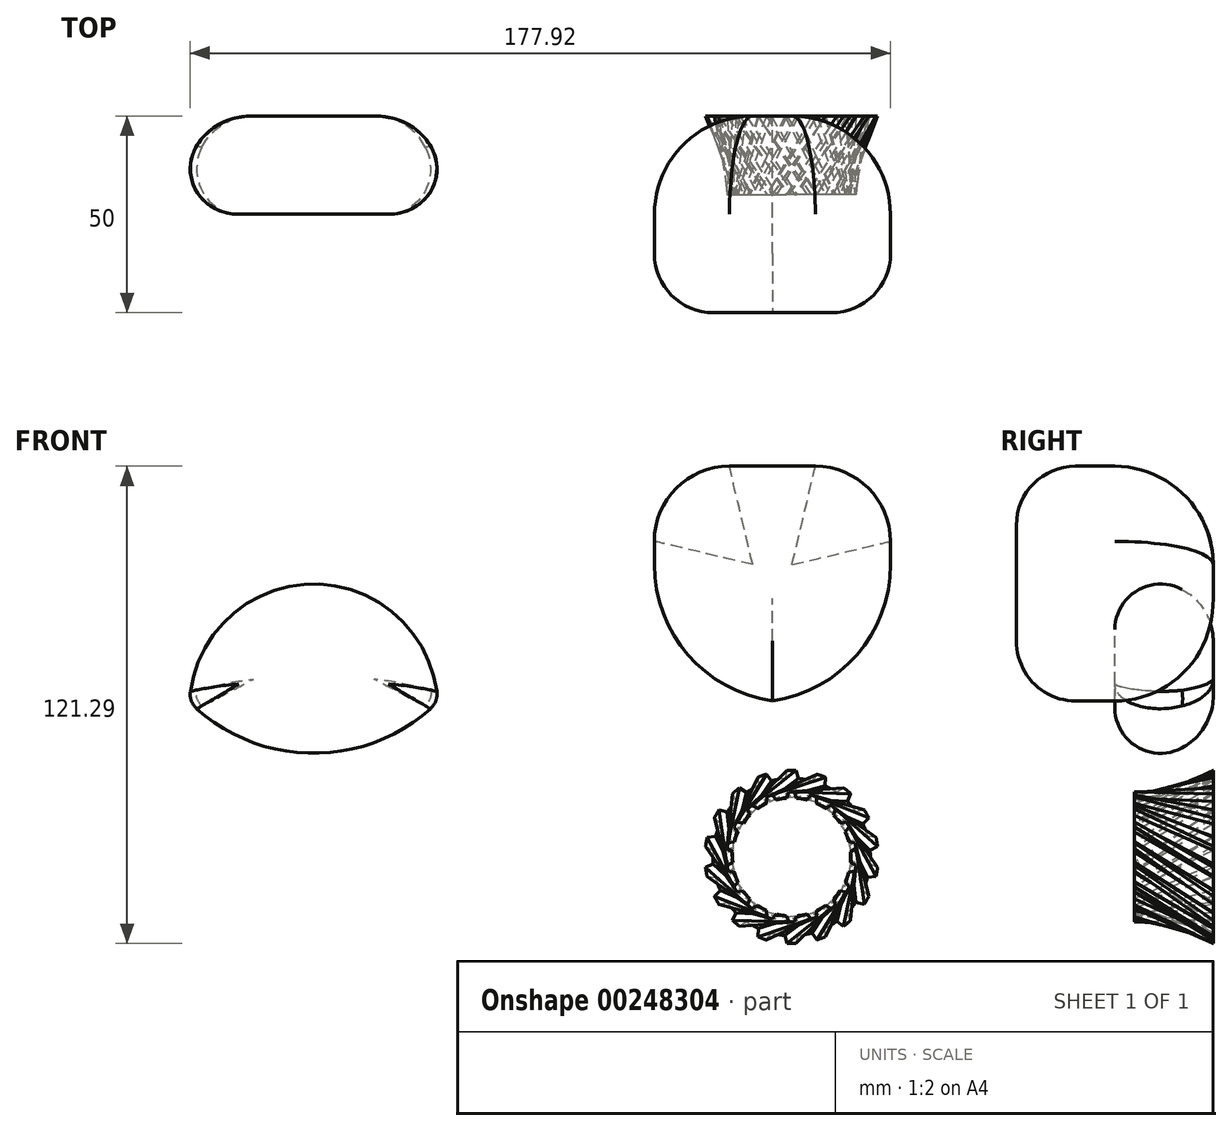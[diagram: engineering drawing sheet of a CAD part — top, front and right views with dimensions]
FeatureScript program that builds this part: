
annotation { "Feature Type Name" : "Feature", "Feature Type Description" : "" }
export const myFeature = defineFeature(function(context is Context, id is Id, definition is map)
    precondition{}
    {
        {
            var Q0;
            Q0=qCreatedBy(makeId("Front.planeOp"),FACE);
            var sketch = newSketch(context, id + "F0", { "sketchPlane" : qUnion([Q0])});
            skLineSegment(sketch, "E0.bottom", {"start": v(0, 0) * mm, "end": v(60, 0) * mm});
            skLineSegment(sketch, "E0.top", {"start": v(0, 40) * mm, "end": v(60, 40) * mm});
            skLineSegment(sketch, "E0.left", {"start": v(0, 0) * mm, "end": v(0, 40) * mm});
            skLineSegment(sketch, "E0.right", {"start": v(60, 0) * mm, "end": v(60, 40) * mm});
            skLineSegment(sketch, "E1.top", {"start": v(0, 60) * mm, "end": v(60, 60) * mm});
            skLineSegment(sketch, "E1.left", {"start": v(0, 40) * mm, "end": v(0, 60) * mm});
            skLineSegment(sketch, "E1.right", {"start": v(60, 40) * mm, "end": v(60, 60) * mm});
            skSolve(sketch);
        }
        {
            var Q0;
            Q0=makeQuery(id+"F0.imprint","IMPRINT",FACE,{"disambiguationData":[TD([[makeQuery(id+"F0.imprint","IMPRINT",EDGE,{"derivedFrom":sQuery(id+"F0.wireOp",EDGE,"E0.bottom")}),1.0]])]});
            extrude(context, id + "F1", {"entities" : qUnion([Q0]), "depth" : 25 * mm});
        }
        {
            var Q0;
            Q0=makeQuery(id+"F1.opExtrude","SWEPT_EDGE",EDGE,{"disambiguationData":[OSD([sQuery(id+"F0.wireOp",EDGE,"E0.bottom"),sQuery(id+"F0.wireOp",EDGE,"E0.right")])]});
            var Q1;
            Q1=makeQuery(id+"F1.opExtrude","SWEPT_EDGE",EDGE,{"disambiguationData":[OSD([sQuery(id+"F0.wireOp",EDGE,"E0.bottom"),sQuery(id+"F0.wireOp",EDGE,"E0.left")])]});
            fillet(context, id + "F2", {"entities" : qUnion([Q0, Q1]), "radius" : 35 * mm, "tangentPropagation" : true, "allowEdgeOverflow" : false});
        }
        {
            var Q0;
            Q0=makeQuery(id+"F0.imprint","IMPRINT",FACE,{"disambiguationData":[TD([[makeQuery(id+"F0.imprint","IMPRINT",EDGE,{"derivedFrom":sQuery(id+"F0.wireOp",EDGE,"E0.top")}),1.0]])]});
            extrude(context, id + "F3", {"entities" : qUnion([Q0]), "depth" : 25 * mm});
        }
        {
            var Q0;
            Q0=makeQuery(id+"F3.opExtrude","SWEPT_EDGE",EDGE,{"disambiguationData":[OSD([sQuery(id+"F0.wireOp",EDGE,"E1.right"),sQuery(id+"F0.wireOp",EDGE,"E1.top"),sQuery(id+"F0.wireOp",EDGE,"npU2ziJ4-tpRD-9A4a-kZAJ-gbLFv57kgjlz.right")])]});
            var Q1;
            Q1=makeQuery(id+"F3.opExtrude","SWEPT_EDGE",EDGE,{"disambiguationData":[OSD([sQuery(id+"F0.wireOp",EDGE,"E1.left"),sQuery(id+"F0.wireOp",EDGE,"E1.top"),sQuery(id+"F0.wireOp",EDGE,"npU2ziJ4-tpRD-9A4a-kZAJ-gbLFv57kgjlz.left")])]});
            fillet(context, id + "F4", {"entities" : qUnion([Q0, Q1]), "radius" : 19.07 * mm, "tangentPropagation" : true, "allowEdgeOverflow" : false});
        }
        {
            var Q0;
            Q0=makeQuery(id+"F3.opExtrude","SWEPT_BODY",BODY,{"disambiguationData":[OSD([sQuery(id+"F0.wireOp",EDGE,"E0.top"),sQuery(id+"F0.wireOp",EDGE,"E1.left"),sQuery(id+"F0.wireOp",EDGE,"E1.right"),sQuery(id+"F0.wireOp",EDGE,"E1.top")])]});
            var Q1;
            Q1=makeQuery(id+"F1.opExtrude","SWEPT_BODY",BODY,{"disambiguationData":[OSD([sQuery(id+"F0.wireOp",EDGE,"E0.bottom"),sQuery(id+"F0.wireOp",EDGE,"E0.left"),sQuery(id+"F0.wireOp",EDGE,"E0.right"),sQuery(id+"F0.wireOp",EDGE,"E0.top")])]});
            booleanBodies(context, id + "F5", {"operationType" : BooleanOperationType.UNION, "tools" : qUnion([Q0, Q1])});
        }
        {
            var Q0;
            Q0=makeQuery(id+"F3.opExtrude","SWEPT_BODY",BODY,{"disambiguationData":[OSD([sQuery(id+"F0.wireOp",EDGE,"E0.top"),sQuery(id+"F0.wireOp",EDGE,"E1.left"),sQuery(id+"F0.wireOp",EDGE,"E1.right"),sQuery(id+"F0.wireOp",EDGE,"E1.top")])]});
            var Q1;
            {var subQ0=sQuery(id+"F0.wireOp",EDGE,"E0.top");Q1=makeQuery(id+"F5.opBoolean","MERGE",FACE,{"derivedFrom":[makeQuery(id+"F1.opExtrude","CAP_FACE",FACE,{"disambiguationData":[OSD([sQuery(id+"F0.wireOp",EDGE,"E0.bottom"),sQuery(id+"F0.wireOp",EDGE,"E0.left"),sQuery(id+"F0.wireOp",EDGE,"E0.right"),subQ0])],"isStart":false}),makeQuery(id+"F3.opExtrude","CAP_FACE",FACE,{"disambiguationData":[OSD([subQ0,sQuery(id+"F0.wireOp",EDGE,"E1.left"),sQuery(id+"F0.wireOp",EDGE,"E1.right"),sQuery(id+"F0.wireOp",EDGE,"E1.top")])],"isStart":false})]});}
            mirror(context, id + "F6", {"operationType" : NewBodyOperationType.ADD, "entities" : qUnion([Q0]), "mirrorPlane" : qUnion([Q1])});
        }
        {
            var Q0;
            {var subQ0=sQuery(id+"F0.wireOp",EDGE,"E0.right");var subQ1=sQuery(id+"F0.wireOp",EDGE,"E0.bottom");Q0=makeQuery(id+"F2.opFillet","BLEND_EDGE",EDGE,{"blendedFrom":[makeQuery(id+"F1.opExtrude","SWEPT_EDGE",EDGE,{"disambiguationData":[OSD([subQ1,subQ0])]}),makeQuery(id+"F1.opExtrude","CAP_FACE",FACE,{"disambiguationData":[OSD([subQ1,sQuery(id+"F0.wireOp",EDGE,"E0.left"),subQ0,sQuery(id+"F0.wireOp",EDGE,"E0.top")])],"isStart":true})],"blendedInto":[makeQuery(id+"F1.opExtrude","CAP_FACE",FACE,{"disambiguationData":[OSD([subQ1,sQuery(id+"F0.wireOp",EDGE,"E0.left"),subQ0,sQuery(id+"F0.wireOp",EDGE,"E0.top")])],"isStart":true})]});}
            var Q1;
            {var subQ0=sQuery(id+"F0.wireOp",EDGE,"E1.top");var subQ1=sQuery(id+"F0.wireOp",EDGE,"E1.right");Q1=makeQuery(id+"F4.opFillet","BLEND_EDGE",EDGE,{"blendedFrom":[makeQuery(id+"F3.opExtrude","SWEPT_EDGE",EDGE,{"disambiguationData":[OSD([subQ1,subQ0,sQuery(id+"F0.wireOp",EDGE,"npU2ziJ4-tpRD-9A4a-kZAJ-gbLFv57kgjlz.right")])]}),makeQuery(id+"F3.opExtrude","CAP_FACE",FACE,{"disambiguationData":[OSD([sQuery(id+"F0.wireOp",EDGE,"E0.top"),sQuery(id+"F0.wireOp",EDGE,"E1.left"),subQ1,subQ0])],"isStart":true})],"blendedInto":[makeQuery(id+"F3.opExtrude","CAP_FACE",FACE,{"disambiguationData":[OSD([sQuery(id+"F0.wireOp",EDGE,"E0.top"),sQuery(id+"F0.wireOp",EDGE,"E1.left"),subQ1,subQ0])],"isStart":true})]});}
            var Q2;
            {var subQ0=sQuery(id+"F0.wireOp",EDGE,"E1.top");var subQ1=sQuery(id+"F0.wireOp",EDGE,"E1.left");Q2=makeQuery(id+"F4.opFillet","BLEND_EDGE",EDGE,{"blendedFrom":[makeQuery(id+"F3.opExtrude","SWEPT_EDGE",EDGE,{"disambiguationData":[OSD([subQ1,subQ0,sQuery(id+"F0.wireOp",EDGE,"npU2ziJ4-tpRD-9A4a-kZAJ-gbLFv57kgjlz.left")])]}),makeQuery(id+"F3.opExtrude","CAP_FACE",FACE,{"disambiguationData":[OSD([sQuery(id+"F0.wireOp",EDGE,"E0.top"),subQ1,sQuery(id+"F0.wireOp",EDGE,"E1.right"),subQ0])],"isStart":true})],"blendedInto":[makeQuery(id+"F3.opExtrude","CAP_FACE",FACE,{"disambiguationData":[OSD([sQuery(id+"F0.wireOp",EDGE,"E0.top"),subQ1,sQuery(id+"F0.wireOp",EDGE,"E1.right"),subQ0])],"isStart":true})]});}
            var Q3;
            {var subQ0=sQuery(id+"F0.wireOp",EDGE,"E0.left");var subQ1=sQuery(id+"F0.wireOp",EDGE,"E0.bottom");Q3=makeQuery(id+"F2.opFillet","BLEND_EDGE",EDGE,{"blendedFrom":[makeQuery(id+"F1.opExtrude","SWEPT_EDGE",EDGE,{"disambiguationData":[OSD([subQ1,subQ0])]}),makeQuery(id+"F1.opExtrude","CAP_FACE",FACE,{"disambiguationData":[OSD([subQ1,subQ0,sQuery(id+"F0.wireOp",EDGE,"E0.right"),sQuery(id+"F0.wireOp",EDGE,"E0.top")])],"isStart":true})],"blendedInto":[makeQuery(id+"F1.opExtrude","CAP_FACE",FACE,{"disambiguationData":[OSD([subQ1,subQ0,sQuery(id+"F0.wireOp",EDGE,"E0.right"),sQuery(id+"F0.wireOp",EDGE,"E0.top")])],"isStart":true})]});}
            fillet(context, id + "F7", {"entities" : qUnion([Q0, Q1, Q2, Q3]), "radius" : 25 * mm, "tangentPropagation" : true, "allowEdgeOverflow" : false});
        }
        {
            var Q0;
            {var subQ0=sQuery(id+"F0.wireOp",EDGE,"E1.top");var subQ1=sQuery(id+"F0.wireOp",EDGE,"E1.right");Q0=makeQuery(id+"F6.opPattern","COPY",EDGE,{"derivedFrom":makeQuery(id+"F4.opFillet","BLEND_EDGE",EDGE,{"blendedFrom":[makeQuery(id+"F3.opExtrude","SWEPT_EDGE",EDGE,{"disambiguationData":[OSD([subQ1,subQ0])]}),makeQuery(id+"F3.opExtrude","CAP_FACE",FACE,{"disambiguationData":[OSD([sQuery(id+"F0.wireOp",EDGE,"E0.top"),sQuery(id+"F0.wireOp",EDGE,"E1.left"),subQ1,subQ0])],"isStart":true})],"blendedInto":[makeQuery(id+"F3.opExtrude","CAP_FACE",FACE,{"disambiguationData":[OSD([sQuery(id+"F0.wireOp",EDGE,"E0.top"),sQuery(id+"F0.wireOp",EDGE,"E1.left"),subQ1,subQ0])],"isStart":true})]}),"instanceName":"1"});}
            var Q1;
            {var subQ0=sQuery(id+"F0.wireOp",EDGE,"E0.right");var subQ1=sQuery(id+"F0.wireOp",EDGE,"E0.bottom");Q1=makeQuery(id+"F6.opPattern","COPY",EDGE,{"derivedFrom":makeQuery(id+"F2.opFillet","BLEND_EDGE",EDGE,{"blendedFrom":[makeQuery(id+"F1.opExtrude","SWEPT_EDGE",EDGE,{"disambiguationData":[OSD([subQ1,subQ0])]}),makeQuery(id+"F1.opExtrude","CAP_FACE",FACE,{"disambiguationData":[OSD([subQ1,sQuery(id+"F0.wireOp",EDGE,"E0.left"),subQ0,sQuery(id+"F0.wireOp",EDGE,"E0.top")])],"isStart":true})],"blendedInto":[makeQuery(id+"F1.opExtrude","CAP_FACE",FACE,{"disambiguationData":[OSD([subQ1,sQuery(id+"F0.wireOp",EDGE,"E0.left"),subQ0,sQuery(id+"F0.wireOp",EDGE,"E0.top")])],"isStart":true})]}),"instanceName":"1"});}
            var Q2;
            {var subQ0=sQuery(id+"F0.wireOp",EDGE,"E0.left");var subQ1=sQuery(id+"F0.wireOp",EDGE,"E0.bottom");Q2=makeQuery(id+"F6.opPattern","COPY",EDGE,{"derivedFrom":makeQuery(id+"F2.opFillet","BLEND_EDGE",EDGE,{"blendedFrom":[makeQuery(id+"F1.opExtrude","SWEPT_EDGE",EDGE,{"disambiguationData":[OSD([subQ1,subQ0])]}),makeQuery(id+"F1.opExtrude","CAP_FACE",FACE,{"disambiguationData":[OSD([subQ1,subQ0,sQuery(id+"F0.wireOp",EDGE,"E0.right"),sQuery(id+"F0.wireOp",EDGE,"E0.top")])],"isStart":true})],"blendedInto":[makeQuery(id+"F1.opExtrude","CAP_FACE",FACE,{"disambiguationData":[OSD([subQ1,subQ0,sQuery(id+"F0.wireOp",EDGE,"E0.right"),sQuery(id+"F0.wireOp",EDGE,"E0.top")])],"isStart":true})]}),"instanceName":"1"});}
            var Q3;
            {var subQ0=sQuery(id+"F0.wireOp",EDGE,"E1.top");var subQ1=sQuery(id+"F0.wireOp",EDGE,"E1.left");Q3=makeQuery(id+"F6.opPattern","COPY",EDGE,{"derivedFrom":makeQuery(id+"F4.opFillet","BLEND_EDGE",EDGE,{"blendedFrom":[makeQuery(id+"F3.opExtrude","SWEPT_EDGE",EDGE,{"disambiguationData":[OSD([subQ1,subQ0])]}),makeQuery(id+"F3.opExtrude","CAP_FACE",FACE,{"disambiguationData":[OSD([sQuery(id+"F0.wireOp",EDGE,"E0.top"),subQ1,sQuery(id+"F0.wireOp",EDGE,"E1.right"),subQ0])],"isStart":true})],"blendedInto":[makeQuery(id+"F3.opExtrude","CAP_FACE",FACE,{"disambiguationData":[OSD([sQuery(id+"F0.wireOp",EDGE,"E0.top"),subQ1,sQuery(id+"F0.wireOp",EDGE,"E1.right"),subQ0])],"isStart":true})]}),"instanceName":"1"});}
            fillet(context, id + "F8", {"entities" : qUnion([Q0, Q1, Q2, Q3]), "radius" : 15 * mm, "tangentPropagation" : true, "allowEdgeOverflow" : false});
        }
        {
            var Q0;
            Q0=qCreatedBy(makeId("Front.planeOp"),FACE);
            var sketch = newSketch(context, id + "F9", { "sketchPlane" : qUnion([Q0])});
            skArc(sketch, "E2", {"start": v(-116.68, -1.76) * mm, "mid": v(-86.56, -13.32) * mm, "end": v(-56.45, -1.76) * mm});
            skArc(sketch, "E3", {"start": v(-54.83, 2.6) * mm, "mid": v(-86.56, 30.45) * mm, "end": v(-118.3, 2.6) * mm});
            skPoint(sketch, "E4.visualSharp", {"position": v(-54.6, 0) * mm});
            skArc(sketch, "E4.filletArc", {"start": v(-56.45, -1.76) * mm, "mid": v(-55.1, 0.22) * mm, "end": v(-54.83, 2.6) * mm});
            skPoint(sketch, "E5.visualSharp", {"position": v(-118.53, 0) * mm});
            skArc(sketch, "E5.filletArc", {"start": v(-118.3, 2.6) * mm, "mid": v(-118.03, 0.22) * mm, "end": v(-116.68, -1.76) * mm});
            skLineSegment(sketch, "E6", {"start": v(-28.6, 0) * mm, "end": v(-153.09, 0) * mm, "construction": true});
            skLineSegment(sketch, "E7", {"start": v(-54.83, 2.6) * mm, "end": v(-54.6, -31.33) * mm, "construction": true});
            skLineSegment(sketch, "E8", {"start": v(-118.3, 2.6) * mm, "end": v(-118.3, -23.9) * mm, "construction": true});
            skSolve(sketch);
        }
        {
            var Q0;
            Q0=makeQuery(id+"F9.imprint","IMPRINT",FACE,{"disambiguationData":[TD([[makeQuery(id+"F9.imprint","IMPRINT",EDGE,{"derivedFrom":sQuery(id+"F9.wireOp",EDGE,"E2")}),1.0]])]});
            extrude(context, id + "F10", {"entities" : qUnion([Q0]), "depth" : 25 * mm});
        }
        {
            var Q0;
            Q0=makeQuery(id+"F10.opExtrude","CAP_EDGE",EDGE,{"disambiguationData":[OSD([sQuery(id+"F9.wireOp",EDGE,"E2")])],"isStart":true});
            var Q1;
            Q1=makeQuery(id+"F10.opExtrude","CAP_EDGE",EDGE,{"disambiguationData":[OSD([sQuery(id+"F9.wireOp",EDGE,"E3")])],"isStart":true});
            fillet(context, id + "F11", {"entities" : qUnion([Q0, Q1]), "radius" : 15 * mm, "tangentPropagation" : true, "allowEdgeOverflow" : false});
        }
        {
            var Q0;
            Q0=makeQuery(id+"F10.opExtrude","CAP_EDGE",EDGE,{"disambiguationData":[OSD([sQuery(id+"F9.wireOp",EDGE,"E3")])],"isStart":false});
            var Q1;
            Q1=makeQuery(id+"F10.opExtrude","CAP_EDGE",EDGE,{"disambiguationData":[OSD([sQuery(id+"F9.wireOp",EDGE,"E2")])],"isStart":false});
            fillet(context, id + "F12", {"entities" : qUnion([Q0, Q1]), "radius" : 11.6 * mm, "tangentPropagation" : true, "allowEdgeOverflow" : false});
        }
        {
            var Q0;
            Q0=qCreatedBy(makeId("Front.planeOp"),FACE);
            var sketch = newSketch(context, id + "F13", { "sketchPlane" : qUnion([Q0])});
            skArc(sketch, "E9", {"start": v(33.13, -19.37) * mm, "mid": v(31.4, -19.6) * mm, "end": v(29.7, -19.98) * mm});
            skArc(sketch, "E10", {"start": v(34.87, -17.3) * mm, "mid": v(34.3, -17.3) * mm, "end": v(33.72, -17.32) * mm});
            skLineSegment(sketch, "E11", {"start": v(34.87, -39.3) * mm, "end": v(34.87, -17.3) * mm, "construction": true});
            skLineSegment(sketch, "E12", {"start": v(34.87, -39.3) * mm, "end": v(33.13, -19.37) * mm, "construction": true});
            skPoint(sketch, "E13", {"position": v(33.72, -17.32) * mm});
            skLineSegment(sketch, "E14", {"start": v(33.72, -17.32) * mm, "end": v(33.13, -19.37) * mm});
            skLineSegment(sketch, "E15.MirrorCS", {"start": v(36.03, -17.32) * mm, "end": v(36.62, -19.37) * mm});
            skArc(sketch, "E16.MirrorCS", {"start": v(34.87, -17.3) * mm, "mid": v(35.45, -17.3) * mm, "end": v(36.03, -17.32) * mm});
            skPoint(sketch, "E17.1.0", {"position": v(26.27, -19.04) * mm});
            skLineSegment(sketch, "E17.1.1", {"start": v(26.27, -19.04) * mm, "end": v(26.42, -21.17) * mm});
            skLineSegment(sketch, "E17.1.2", {"start": v(28.44, -18.25) * mm, "end": v(29.7, -19.98) * mm});
            skArc(sketch, "E17.1.3", {"start": v(27.35, -18.62) * mm, "mid": v(26.8, -18.83) * mm, "end": v(26.27, -19.04) * mm});
            skArc(sketch, "E17.1.4", {"start": v(27.35, -18.62) * mm, "mid": v(27.9, -18.43) * mm, "end": v(28.44, -18.25) * mm});
            skPoint(sketch, "E17.2.0", {"position": v(19.86, -23.2) * mm});
            skLineSegment(sketch, "E17.2.1", {"start": v(19.86, -23.2) * mm, "end": v(20.73, -25.15) * mm});
            skLineSegment(sketch, "E17.2.2", {"start": v(21.64, -21.72) * mm, "end": v(23.4, -22.91) * mm});
            skArc(sketch, "E17.2.3", {"start": v(20.73, -22.44) * mm, "mid": v(20.3, -22.82) * mm, "end": v(19.86, -23.2) * mm});
            skArc(sketch, "E17.2.4", {"start": v(20.73, -22.44) * mm, "mid": v(21.18, -22.08) * mm, "end": v(21.64, -21.72) * mm});
            skPoint(sketch, "E17.3.0", {"position": v(15.27, -29.31) * mm});
            skLineSegment(sketch, "E17.3.1", {"start": v(15.27, -29.31) * mm, "end": v(16.75, -30.84) * mm});
            skLineSegment(sketch, "E17.3.2", {"start": v(16.42, -27.3) * mm, "end": v(18.49, -27.82) * mm});
            skArc(sketch, "E17.3.3", {"start": v(15.82, -28.3) * mm, "mid": v(15.54, -28.8) * mm, "end": v(15.27, -29.31) * mm});
            skArc(sketch, "E17.3.4", {"start": v(15.82, -28.3) * mm, "mid": v(16.12, -27.8) * mm, "end": v(16.42, -27.3) * mm});
            skPoint(sketch, "E17.4.0", {"position": v(13.04, -36.62) * mm});
            skLineSegment(sketch, "E17.4.1", {"start": v(13.04, -36.62) * mm, "end": v(14.95, -37.55) * mm});
            skLineSegment(sketch, "E17.4.2", {"start": v(13.44, -34.34) * mm, "end": v(15.55, -34.12) * mm});
            skArc(sketch, "E17.4.3", {"start": v(13.2, -35.47) * mm, "mid": v(13.11, -36.04) * mm, "end": v(13.04, -36.62) * mm});
            skArc(sketch, "E17.4.4", {"start": v(13.2, -35.47) * mm, "mid": v(13.31, -34.9) * mm, "end": v(13.44, -34.34) * mm});
            skPoint(sketch, "E17.5.0", {"position": v(13.44, -44.25) * mm});
            skLineSegment(sketch, "E17.5.1", {"start": v(13.44, -44.25) * mm, "end": v(15.55, -44.47) * mm});
            skLineSegment(sketch, "E17.5.2", {"start": v(13.04, -41.97) * mm, "end": v(14.95, -41.04) * mm});
            skArc(sketch, "E17.5.3", {"start": v(13.2, -43.11) * mm, "mid": v(13.31, -43.68) * mm, "end": v(13.44, -44.25) * mm});
            skArc(sketch, "E17.5.4", {"start": v(13.2, -43.11) * mm, "mid": v(13.11, -42.54) * mm, "end": v(13.04, -41.97) * mm});
            skPoint(sketch, "E17.6.0", {"position": v(16.42, -51.28) * mm});
            skLineSegment(sketch, "E17.6.1", {"start": v(16.42, -51.28) * mm, "end": v(18.49, -50.77) * mm});
            skLineSegment(sketch, "E17.6.2", {"start": v(15.27, -49.28) * mm, "end": v(16.75, -47.75) * mm});
            skArc(sketch, "E17.6.3", {"start": v(15.82, -50.3) * mm, "mid": v(16.12, -50.8) * mm, "end": v(16.42, -51.28) * mm});
            skArc(sketch, "E17.6.4", {"start": v(15.82, -50.3) * mm, "mid": v(15.54, -49.79) * mm, "end": v(15.27, -49.28) * mm});
            skPoint(sketch, "E17.7.0", {"position": v(21.64, -56.87) * mm});
            skLineSegment(sketch, "E17.7.1", {"start": v(21.64, -56.87) * mm, "end": v(23.4, -55.68) * mm});
            skLineSegment(sketch, "E17.7.2", {"start": v(19.86, -55.38) * mm, "end": v(20.73, -53.44) * mm});
            skArc(sketch, "E17.7.3", {"start": v(20.73, -56.15) * mm, "mid": v(21.18, -56.51) * mm, "end": v(21.64, -56.87) * mm});
            skArc(sketch, "E17.7.4", {"start": v(20.73, -56.15) * mm, "mid": v(20.3, -55.77) * mm, "end": v(19.86, -55.38) * mm});
            skPoint(sketch, "E17.8.0", {"position": v(28.44, -60.33) * mm});
            skLineSegment(sketch, "E17.8.1", {"start": v(28.44, -60.33) * mm, "end": v(29.7, -58.61) * mm});
            skLineSegment(sketch, "E17.8.2", {"start": v(26.27, -59.54) * mm, "end": v(26.42, -57.42) * mm});
            skArc(sketch, "E17.8.3", {"start": v(27.35, -59.97) * mm, "mid": v(27.9, -60.16) * mm, "end": v(28.44, -60.33) * mm});
            skArc(sketch, "E17.8.4", {"start": v(27.35, -59.97) * mm, "mid": v(26.8, -59.76) * mm, "end": v(26.27, -59.54) * mm});
            skPoint(sketch, "E17.9.0", {"position": v(36.03, -61.26) * mm});
            skLineSegment(sketch, "E17.9.1", {"start": v(36.03, -61.26) * mm, "end": v(36.62, -59.22) * mm});
            skLineSegment(sketch, "E17.9.2", {"start": v(33.72, -61.26) * mm, "end": v(33.13, -59.22) * mm});
            skArc(sketch, "E17.9.3", {"start": v(34.87, -61.3) * mm, "mid": v(35.45, -61.29) * mm, "end": v(36.03, -61.26) * mm});
            skArc(sketch, "E17.9.4", {"start": v(34.87, -61.3) * mm, "mid": v(34.3, -61.29) * mm, "end": v(33.72, -61.26) * mm});
            skPoint(sketch, "E17.10.0", {"position": v(43.47, -59.54) * mm});
            skLineSegment(sketch, "E17.10.1", {"start": v(43.47, -59.54) * mm, "end": v(43.32, -57.42) * mm});
            skLineSegment(sketch, "E17.10.2", {"start": v(41.3, -60.33) * mm, "end": v(40.05, -58.61) * mm});
            skArc(sketch, "E17.10.3", {"start": v(42.4, -59.97) * mm, "mid": v(42.94, -59.76) * mm, "end": v(43.47, -59.54) * mm});
            skArc(sketch, "E17.10.4", {"start": v(42.4, -59.97) * mm, "mid": v(41.85, -60.16) * mm, "end": v(41.3, -60.33) * mm});
            skPoint(sketch, "E17.11.0", {"position": v(49.88, -55.38) * mm});
            skLineSegment(sketch, "E17.11.1", {"start": v(49.88, -55.38) * mm, "end": v(49.01, -53.44) * mm});
            skLineSegment(sketch, "E17.11.2", {"start": v(48.1, -56.87) * mm, "end": v(46.34, -55.68) * mm});
            skArc(sketch, "E17.11.3", {"start": v(49.01, -56.15) * mm, "mid": v(49.45, -55.77) * mm, "end": v(49.88, -55.38) * mm});
            skArc(sketch, "E17.11.4", {"start": v(49.01, -56.15) * mm, "mid": v(48.57, -56.51) * mm, "end": v(48.1, -56.87) * mm});
            skPoint(sketch, "E17.12.0", {"position": v(54.48, -49.28) * mm});
            skLineSegment(sketch, "E17.12.1", {"start": v(54.48, -49.28) * mm, "end": v(53, -47.75) * mm});
            skLineSegment(sketch, "E17.12.2", {"start": v(53.32, -51.28) * mm, "end": v(51.26, -50.77) * mm});
            skArc(sketch, "E17.12.3", {"start": v(53.92, -50.3) * mm, "mid": v(54.2, -49.79) * mm, "end": v(54.48, -49.28) * mm});
            skArc(sketch, "E17.12.4", {"start": v(53.92, -50.3) * mm, "mid": v(53.63, -50.8) * mm, "end": v(53.32, -51.28) * mm});
            skPoint(sketch, "E17.13.0", {"position": v(56.7, -41.97) * mm});
            skLineSegment(sketch, "E17.13.1", {"start": v(56.7, -41.97) * mm, "end": v(54.8, -41.04) * mm});
            skLineSegment(sketch, "E17.13.2", {"start": v(56.3, -44.25) * mm, "end": v(54.2, -44.47) * mm});
            skArc(sketch, "E17.13.3", {"start": v(56.54, -43.11) * mm, "mid": v(56.63, -42.54) * mm, "end": v(56.7, -41.97) * mm});
            skArc(sketch, "E17.13.4", {"start": v(56.54, -43.11) * mm, "mid": v(56.43, -43.68) * mm, "end": v(56.3, -44.25) * mm});
            skPoint(sketch, "E17.14.0", {"position": v(56.3, -34.34) * mm});
            skLineSegment(sketch, "E17.14.1", {"start": v(56.3, -34.34) * mm, "end": v(54.2, -34.12) * mm});
            skLineSegment(sketch, "E17.14.2", {"start": v(56.7, -36.62) * mm, "end": v(54.8, -37.55) * mm});
            skArc(sketch, "E17.14.3", {"start": v(56.54, -35.47) * mm, "mid": v(56.43, -34.9) * mm, "end": v(56.3, -34.34) * mm});
            skArc(sketch, "E17.14.4", {"start": v(56.54, -35.47) * mm, "mid": v(56.63, -36.04) * mm, "end": v(56.7, -36.62) * mm});
            skPoint(sketch, "E17.15.0", {"position": v(53.32, -27.3) * mm});
            skLineSegment(sketch, "E17.15.1", {"start": v(53.32, -27.3) * mm, "end": v(51.26, -27.82) * mm});
            skLineSegment(sketch, "E17.15.2", {"start": v(54.48, -29.31) * mm, "end": v(53, -30.84) * mm});
            skArc(sketch, "E17.15.3", {"start": v(53.92, -28.3) * mm, "mid": v(53.63, -27.8) * mm, "end": v(53.32, -27.3) * mm});
            skArc(sketch, "E17.15.4", {"start": v(53.92, -28.3) * mm, "mid": v(54.2, -28.8) * mm, "end": v(54.48, -29.31) * mm});
            skPoint(sketch, "E17.16.0", {"position": v(48.1, -21.72) * mm});
            skLineSegment(sketch, "E17.16.1", {"start": v(48.1, -21.72) * mm, "end": v(46.34, -22.91) * mm});
            skLineSegment(sketch, "E17.16.2", {"start": v(49.88, -23.2) * mm, "end": v(49.01, -25.15) * mm});
            skArc(sketch, "E17.16.3", {"start": v(49.01, -22.44) * mm, "mid": v(48.57, -22.08) * mm, "end": v(48.1, -21.72) * mm});
            skArc(sketch, "E17.16.4", {"start": v(49.01, -22.44) * mm, "mid": v(49.45, -22.82) * mm, "end": v(49.88, -23.2) * mm});
            skPoint(sketch, "E17.17.0", {"position": v(41.3, -18.25) * mm});
            skLineSegment(sketch, "E17.17.1", {"start": v(41.3, -18.25) * mm, "end": v(40.05, -19.98) * mm});
            skLineSegment(sketch, "E17.17.2", {"start": v(43.47, -19.04) * mm, "end": v(43.32, -21.17) * mm});
            skArc(sketch, "E17.17.3", {"start": v(42.4, -18.62) * mm, "mid": v(41.85, -18.43) * mm, "end": v(41.3, -18.25) * mm});
            skArc(sketch, "E17.17.4", {"start": v(42.4, -18.62) * mm, "mid": v(42.94, -18.83) * mm, "end": v(43.47, -19.04) * mm});
            skArc(sketch, "E18.trimOffspring", {"start": v(40.05, -19.98) * mm, "mid": v(38.35, -19.6) * mm, "end": v(36.62, -19.37) * mm});
            skArc(sketch, "E19.trimOffspring", {"start": v(46.34, -22.91) * mm, "mid": v(44.87, -21.97) * mm, "end": v(43.32, -21.17) * mm});
            skArc(sketch, "E20.trimOffspring", {"start": v(51.26, -27.82) * mm, "mid": v(50.2, -26.44) * mm, "end": v(49.01, -25.15) * mm});
            skArc(sketch, "E21.trimOffspring", {"start": v(54.2, -34.12) * mm, "mid": v(53.67, -32.45) * mm, "end": v(53, -30.84) * mm});
            skArc(sketch, "E22.trimOffspring", {"start": v(54.8, -41.04) * mm, "mid": v(54.87, -39.3) * mm, "end": v(54.8, -37.55) * mm});
            skArc(sketch, "E23.trimOffspring", {"start": v(53, -47.75) * mm, "mid": v(53.67, -46.13) * mm, "end": v(54.2, -44.47) * mm});
            skArc(sketch, "E24.trimOffspring", {"start": v(49.01, -53.44) * mm, "mid": v(50.2, -52.15) * mm, "end": v(51.26, -50.77) * mm});
            skArc(sketch, "E25.trimOffspring", {"start": v(43.32, -57.42) * mm, "mid": v(44.87, -56.61) * mm, "end": v(46.34, -55.68) * mm});
            skArc(sketch, "E26.trimOffspring", {"start": v(36.62, -59.22) * mm, "mid": v(38.35, -59) * mm, "end": v(40.05, -58.61) * mm});
            skArc(sketch, "E27.trimOffspring", {"start": v(29.7, -58.61) * mm, "mid": v(31.4, -59) * mm, "end": v(33.13, -59.22) * mm});
            skArc(sketch, "E28.trimOffspring", {"start": v(23.4, -55.68) * mm, "mid": v(24.87, -56.61) * mm, "end": v(26.42, -57.42) * mm});
            skArc(sketch, "E29.trimOffspring", {"start": v(18.49, -50.77) * mm, "mid": v(19.55, -52.15) * mm, "end": v(20.73, -53.44) * mm});
            skArc(sketch, "E30.trimOffspring", {"start": v(15.55, -44.47) * mm, "mid": v(16.08, -46.13) * mm, "end": v(16.75, -47.75) * mm});
            skArc(sketch, "E31.trimOffspring", {"start": v(14.95, -37.55) * mm, "mid": v(14.87, -39.3) * mm, "end": v(14.95, -41.04) * mm});
            skArc(sketch, "E32.trimOffspring", {"start": v(16.75, -30.84) * mm, "mid": v(16.08, -32.45) * mm, "end": v(15.55, -34.12) * mm});
            skArc(sketch, "E33.trimOffspring", {"start": v(20.73, -25.15) * mm, "mid": v(19.55, -26.44) * mm, "end": v(18.49, -27.82) * mm});
            skArc(sketch, "E34.trimOffspring", {"start": v(26.42, -21.17) * mm, "mid": v(24.87, -21.97) * mm, "end": v(23.4, -22.91) * mm});
            skSolve(sketch);
        }
        {
            var Q0;
            Q0=qCreatedBy(makeId("Front.planeOp"),FACE);
            cPlane(context, id + "F14", {"entities" : qUnion([Q0]), "cplaneType" : CPlaneType.OFFSET, "offset" : 20 * mm, "width" : 150 * mm, "height" : 150 * mm});
        }
        {
            var Q0;
            Q0=qCreatedBy(id+"F14.planeOp",FACE);
            var sketch = newSketch(context, id + "F15", { "sketchPlane" : qUnion([Q0])});
            skPoint(sketch, "E35.0", {"position": v(34.87, -39.3) * mm});
            skArc(sketch, "E36", {"start": v(33.56, -24.35) * mm, "mid": v(32.27, -24.52) * mm, "end": v(30.99, -24.8) * mm});
            skArc(sketch, "E37", {"start": v(34.87, -22.8) * mm, "mid": v(34.51, -22.8) * mm, "end": v(34.15, -22.8) * mm});
            skLineSegment(sketch, "E38.0", {"start": v(34.87, -39.3) * mm, "end": v(34.87, -17.3) * mm, "construction": true});
            skLineSegment(sketch, "E39.0", {"start": v(34.87, -39.3) * mm, "end": v(33.13, -19.37) * mm, "construction": true});
            skPoint(sketch, "E40", {"position": v(34.15, -22.8) * mm});
            skLineSegment(sketch, "E41", {"start": v(34.15, -22.8) * mm, "end": v(33.56, -24.35) * mm});
            skLineSegment(sketch, "E42.MirrorCS", {"start": v(35.6, -22.8) * mm, "end": v(36.18, -24.35) * mm});
            skArc(sketch, "E43.MirrorCS", {"start": v(34.87, -22.8) * mm, "mid": v(35.23, -22.8) * mm, "end": v(35.6, -22.8) * mm});
            skLineSegment(sketch, "E44.1.0", {"start": v(29.91, -23.56) * mm, "end": v(30.99, -24.8) * mm});
            skLineSegment(sketch, "E44.1.1", {"start": v(28.56, -24.05) * mm, "end": v(28.53, -25.7) * mm});
            skArc(sketch, "E44.1.2", {"start": v(29.23, -23.79) * mm, "mid": v(29.57, -23.67) * mm, "end": v(29.91, -23.56) * mm});
            skArc(sketch, "E44.1.3", {"start": v(29.23, -23.79) * mm, "mid": v(28.9, -23.92) * mm, "end": v(28.56, -24.05) * mm});
            skPoint(sketch, "E44.1.4", {"position": v(28.56, -24.05) * mm});
            skLineSegment(sketch, "E44.2.0", {"start": v(24.83, -26.2) * mm, "end": v(26.27, -27) * mm});
            skLineSegment(sketch, "E44.2.1", {"start": v(23.72, -27.13) * mm, "end": v(24.27, -28.69) * mm});
            skArc(sketch, "E44.2.2", {"start": v(24.27, -26.65) * mm, "mid": v(24.54, -26.43) * mm, "end": v(24.83, -26.2) * mm});
            skArc(sketch, "E44.2.3", {"start": v(24.27, -26.65) * mm, "mid": v(24, -26.89) * mm, "end": v(23.72, -27.13) * mm});
            skPoint(sketch, "E44.2.4", {"position": v(23.72, -27.13) * mm});
            skLineSegment(sketch, "E44.3.0", {"start": v(20.96, -30.43) * mm, "end": v(22.58, -30.7) * mm});
            skLineSegment(sketch, "E44.3.1", {"start": v(20.24, -31.68) * mm, "end": v(21.28, -32.95) * mm});
            skArc(sketch, "E44.3.2", {"start": v(20.58, -31.04) * mm, "mid": v(20.77, -30.73) * mm, "end": v(20.96, -30.43) * mm});
            skArc(sketch, "E44.3.3", {"start": v(20.58, -31.04) * mm, "mid": v(20.4, -31.36) * mm, "end": v(20.24, -31.68) * mm});
            skPoint(sketch, "E44.3.4", {"position": v(20.24, -31.68) * mm});
            skLineSegment(sketch, "E44.4.0", {"start": v(18.76, -35.72) * mm, "end": v(20.38, -35.41) * mm});
            skLineSegment(sketch, "E44.4.1", {"start": v(18.51, -37.14) * mm, "end": v(19.93, -37.99) * mm});
            skArc(sketch, "E44.4.2", {"start": v(18.62, -36.43) * mm, "mid": v(18.69, -36.08) * mm, "end": v(18.76, -35.72) * mm});
            skArc(sketch, "E44.4.3", {"start": v(18.62, -36.43) * mm, "mid": v(18.56, -36.78) * mm, "end": v(18.51, -37.14) * mm});
            skPoint(sketch, "E44.4.4", {"position": v(18.51, -37.14) * mm});
            skLineSegment(sketch, "E44.5.0", {"start": v(18.51, -41.45) * mm, "end": v(19.93, -40.6) * mm});
            skLineSegment(sketch, "E44.5.1", {"start": v(18.76, -42.87) * mm, "end": v(20.38, -43.18) * mm});
            skArc(sketch, "E44.5.2", {"start": v(18.62, -42.16) * mm, "mid": v(18.56, -41.8) * mm, "end": v(18.51, -41.45) * mm});
            skArc(sketch, "E44.5.3", {"start": v(18.62, -42.16) * mm, "mid": v(18.69, -42.51) * mm, "end": v(18.76, -42.87) * mm});
            skPoint(sketch, "E44.5.4", {"position": v(18.76, -42.87) * mm});
            skLineSegment(sketch, "E44.6.0", {"start": v(20.24, -46.91) * mm, "end": v(21.28, -45.63) * mm});
            skLineSegment(sketch, "E44.6.1", {"start": v(20.96, -48.16) * mm, "end": v(22.58, -47.9) * mm});
            skArc(sketch, "E44.6.2", {"start": v(20.58, -47.54) * mm, "mid": v(20.4, -47.23) * mm, "end": v(20.24, -46.91) * mm});
            skArc(sketch, "E44.6.3", {"start": v(20.58, -47.54) * mm, "mid": v(20.77, -47.85) * mm, "end": v(20.96, -48.16) * mm});
            skPoint(sketch, "E44.6.4", {"position": v(20.96, -48.16) * mm});
            skLineSegment(sketch, "E44.7.0", {"start": v(23.72, -51.46) * mm, "end": v(24.27, -49.9) * mm});
            skLineSegment(sketch, "E44.7.1", {"start": v(24.83, -52.38) * mm, "end": v(26.27, -51.58) * mm});
            skArc(sketch, "E44.7.2", {"start": v(24.27, -51.93) * mm, "mid": v(24, -51.7) * mm, "end": v(23.72, -51.46) * mm});
            skArc(sketch, "E44.7.3", {"start": v(24.27, -51.93) * mm, "mid": v(24.54, -52.16) * mm, "end": v(24.83, -52.38) * mm});
            skPoint(sketch, "E44.7.4", {"position": v(24.83, -52.38) * mm});
            skLineSegment(sketch, "E44.8.0", {"start": v(28.56, -54.54) * mm, "end": v(28.53, -52.89) * mm});
            skLineSegment(sketch, "E44.8.1", {"start": v(29.91, -55.03) * mm, "end": v(30.99, -53.78) * mm});
            skArc(sketch, "E44.8.2", {"start": v(29.23, -54.8) * mm, "mid": v(28.9, -54.67) * mm, "end": v(28.56, -54.54) * mm});
            skArc(sketch, "E44.8.3", {"start": v(29.23, -54.8) * mm, "mid": v(29.57, -54.92) * mm, "end": v(29.91, -55.03) * mm});
            skPoint(sketch, "E44.8.4", {"position": v(29.91, -55.03) * mm});
            skLineSegment(sketch, "E44.9.0", {"start": v(34.15, -55.78) * mm, "end": v(33.56, -54.24) * mm});
            skLineSegment(sketch, "E44.9.1", {"start": v(35.6, -55.78) * mm, "end": v(36.18, -54.24) * mm});
            skArc(sketch, "E44.9.2", {"start": v(34.87, -55.8) * mm, "mid": v(34.51, -55.8) * mm, "end": v(34.15, -55.78) * mm});
            skArc(sketch, "E44.9.3", {"start": v(34.87, -55.8) * mm, "mid": v(35.23, -55.8) * mm, "end": v(35.6, -55.78) * mm});
            skPoint(sketch, "E44.9.4", {"position": v(35.6, -55.78) * mm});
            skLineSegment(sketch, "E44.10.0", {"start": v(39.83, -55.03) * mm, "end": v(38.75, -53.78) * mm});
            skLineSegment(sketch, "E44.10.1", {"start": v(41.19, -54.54) * mm, "end": v(41.21, -52.89) * mm});
            skArc(sketch, "E44.10.2", {"start": v(40.52, -54.8) * mm, "mid": v(40.18, -54.92) * mm, "end": v(39.83, -55.03) * mm});
            skArc(sketch, "E44.10.3", {"start": v(40.52, -54.8) * mm, "mid": v(40.85, -54.67) * mm, "end": v(41.19, -54.54) * mm});
            skPoint(sketch, "E44.10.4", {"position": v(41.19, -54.54) * mm});
            skLineSegment(sketch, "E44.11.0", {"start": v(44.92, -52.38) * mm, "end": v(43.48, -51.58) * mm});
            skLineSegment(sketch, "E44.11.1", {"start": v(46.02, -51.46) * mm, "end": v(45.48, -49.9) * mm});
            skArc(sketch, "E44.11.2", {"start": v(45.48, -51.93) * mm, "mid": v(45.2, -52.16) * mm, "end": v(44.92, -52.38) * mm});
            skArc(sketch, "E44.11.3", {"start": v(45.48, -51.93) * mm, "mid": v(45.75, -51.7) * mm, "end": v(46.02, -51.46) * mm});
            skPoint(sketch, "E44.11.4", {"position": v(46.02, -51.46) * mm});
            skLineSegment(sketch, "E44.12.0", {"start": v(48.79, -48.16) * mm, "end": v(47.16, -47.9) * mm});
            skLineSegment(sketch, "E44.12.1", {"start": v(49.5, -46.91) * mm, "end": v(48.47, -45.63) * mm});
            skArc(sketch, "E44.12.2", {"start": v(49.16, -47.54) * mm, "mid": v(48.98, -47.85) * mm, "end": v(48.79, -48.16) * mm});
            skArc(sketch, "E44.12.3", {"start": v(49.16, -47.54) * mm, "mid": v(49.34, -47.23) * mm, "end": v(49.5, -46.91) * mm});
            skPoint(sketch, "E44.12.4", {"position": v(49.5, -46.91) * mm});
            skLineSegment(sketch, "E44.13.0", {"start": v(50.98, -42.87) * mm, "end": v(49.36, -43.18) * mm});
            skLineSegment(sketch, "E44.13.1", {"start": v(51.23, -41.45) * mm, "end": v(49.82, -40.6) * mm});
            skArc(sketch, "E44.13.2", {"start": v(51.12, -42.16) * mm, "mid": v(51.06, -42.51) * mm, "end": v(50.98, -42.87) * mm});
            skArc(sketch, "E44.13.3", {"start": v(51.12, -42.16) * mm, "mid": v(51.18, -41.8) * mm, "end": v(51.23, -41.45) * mm});
            skPoint(sketch, "E44.13.4", {"position": v(51.23, -41.45) * mm});
            skLineSegment(sketch, "E44.14.0", {"start": v(51.23, -37.14) * mm, "end": v(49.82, -37.99) * mm});
            skLineSegment(sketch, "E44.14.1", {"start": v(50.98, -35.72) * mm, "end": v(49.36, -35.41) * mm});
            skArc(sketch, "E44.14.2", {"start": v(51.12, -36.43) * mm, "mid": v(51.18, -36.78) * mm, "end": v(51.23, -37.14) * mm});
            skArc(sketch, "E44.14.3", {"start": v(51.12, -36.43) * mm, "mid": v(51.06, -36.08) * mm, "end": v(50.98, -35.72) * mm});
            skPoint(sketch, "E44.14.4", {"position": v(50.98, -35.72) * mm});
            skLineSegment(sketch, "E44.15.0", {"start": v(49.5, -31.68) * mm, "end": v(48.47, -32.95) * mm});
            skLineSegment(sketch, "E44.15.1", {"start": v(48.79, -30.43) * mm, "end": v(47.16, -30.7) * mm});
            skArc(sketch, "E44.15.2", {"start": v(49.16, -31.04) * mm, "mid": v(49.34, -31.36) * mm, "end": v(49.5, -31.68) * mm});
            skArc(sketch, "E44.15.3", {"start": v(49.16, -31.04) * mm, "mid": v(48.98, -30.73) * mm, "end": v(48.79, -30.43) * mm});
            skPoint(sketch, "E44.15.4", {"position": v(48.79, -30.43) * mm});
            skLineSegment(sketch, "E44.16.0", {"start": v(46.02, -27.13) * mm, "end": v(45.48, -28.69) * mm});
            skLineSegment(sketch, "E44.16.1", {"start": v(44.92, -26.2) * mm, "end": v(43.48, -27) * mm});
            skArc(sketch, "E44.16.2", {"start": v(45.48, -26.65) * mm, "mid": v(45.75, -26.89) * mm, "end": v(46.02, -27.13) * mm});
            skArc(sketch, "E44.16.3", {"start": v(45.48, -26.65) * mm, "mid": v(45.2, -26.43) * mm, "end": v(44.92, -26.2) * mm});
            skPoint(sketch, "E44.16.4", {"position": v(44.92, -26.2) * mm});
            skLineSegment(sketch, "E44.17.0", {"start": v(41.19, -24.05) * mm, "end": v(41.21, -25.7) * mm});
            skLineSegment(sketch, "E44.17.1", {"start": v(39.83, -23.56) * mm, "end": v(38.75, -24.8) * mm});
            skArc(sketch, "E44.17.2", {"start": v(40.52, -23.79) * mm, "mid": v(40.85, -23.92) * mm, "end": v(41.19, -24.05) * mm});
            skArc(sketch, "E44.17.3", {"start": v(40.52, -23.79) * mm, "mid": v(40.18, -23.67) * mm, "end": v(39.83, -23.56) * mm});
            skPoint(sketch, "E44.17.4", {"position": v(39.83, -23.56) * mm});
            skArc(sketch, "E45.trimOffspring", {"start": v(28.53, -25.7) * mm, "mid": v(27.37, -26.3) * mm, "end": v(26.27, -27) * mm});
            skArc(sketch, "E46.trimOffspring", {"start": v(24.27, -28.69) * mm, "mid": v(23.38, -29.65) * mm, "end": v(22.58, -30.7) * mm});
            skArc(sketch, "E47.trimOffspring", {"start": v(21.28, -32.95) * mm, "mid": v(20.78, -34.16) * mm, "end": v(20.38, -35.41) * mm});
            skArc(sketch, "E48.trimOffspring", {"start": v(19.93, -37.99) * mm, "mid": v(19.87, -39.3) * mm, "end": v(19.93, -40.6) * mm});
            skArc(sketch, "E49.trimOffspring", {"start": v(22.58, -47.9) * mm, "mid": v(23.38, -48.94) * mm, "end": v(24.27, -49.9) * mm});
            skArc(sketch, "E50.trimOffspring", {"start": v(30.99, -53.78) * mm, "mid": v(32.27, -54.07) * mm, "end": v(33.56, -54.24) * mm});
            skArc(sketch, "E51.trimOffspring", {"start": v(26.27, -51.58) * mm, "mid": v(27.37, -52.28) * mm, "end": v(28.53, -52.89) * mm});
            skArc(sketch, "E52.trimOffspring", {"start": v(36.18, -54.24) * mm, "mid": v(37.48, -54.07) * mm, "end": v(38.75, -53.78) * mm});
            skArc(sketch, "E53.trimOffspring", {"start": v(45.48, -49.9) * mm, "mid": v(46.36, -48.94) * mm, "end": v(47.16, -47.9) * mm});
            skArc(sketch, "E54.trimOffspring", {"start": v(48.47, -45.63) * mm, "mid": v(48.97, -44.42) * mm, "end": v(49.36, -43.18) * mm});
            skArc(sketch, "E55.trimOffspring", {"start": v(49.82, -40.6) * mm, "mid": v(49.87, -39.3) * mm, "end": v(49.82, -37.99) * mm});
            skArc(sketch, "E56.trimOffspring", {"start": v(49.36, -35.41) * mm, "mid": v(48.97, -34.16) * mm, "end": v(48.47, -32.95) * mm});
            skArc(sketch, "E57.trimOffspring", {"start": v(47.16, -30.7) * mm, "mid": v(46.36, -29.65) * mm, "end": v(45.48, -28.69) * mm});
            skArc(sketch, "E58.trimOffspring", {"start": v(43.48, -27) * mm, "mid": v(42.37, -26.3) * mm, "end": v(41.21, -25.7) * mm});
            skArc(sketch, "E59.trimOffspring", {"start": v(38.75, -24.8) * mm, "mid": v(37.48, -24.52) * mm, "end": v(36.18, -24.35) * mm});
            skArc(sketch, "E60", {"start": v(20.38, -43.18) * mm, "mid": v(20.78, -44.42) * mm, "end": v(21.28, -45.63) * mm});
            skArc(sketch, "E61", {"start": v(41.21, -52.89) * mm, "mid": v(42.37, -52.28) * mm, "end": v(43.48, -51.58) * mm});
            skSolve(sketch);
        }
        {
            var Q0;
            Q0=makeQuery(id+"F13.imprint","IMPRINT",FACE,{"disambiguationData":[TD([[makeQuery(id+"F13.imprint","IMPRINT",EDGE,{"derivedFrom":sQuery(id+"F13.wireOp",EDGE,"E9")}),1.0]])]});
            var Q1;
            Q1=makeQuery(id+"F15.imprint","IMPRINT",FACE,{"disambiguationData":[TD([[makeQuery(id+"F15.imprint","IMPRINT",EDGE,{"derivedFrom":sQuery(id+"F15.wireOp",EDGE,"E36")}),1.0]])]});
            var Q2;
            Q2=sQuery(id+"F15.wireOp",VERTEX,"E50.trimOffspring.end");
            var Q3;
            Q3=sQuery(id+"F13.wireOp",VERTEX,"E17.7.2.end");
            loft(context, id + "F16", {"sheetProfilesArray" : [{ "sheetProfileEntities" : qUnion([Q0]) }, { "sheetProfileEntities" : qUnion([Q1]) }], "matchConnections" : true, "connections" : [{ "connectionEntities" : qUnion([Q2, Q3]), "connectionEdgeQueries" : qUnion([]), "connectionEdgeParameters" : [] }]});
        }
    });
